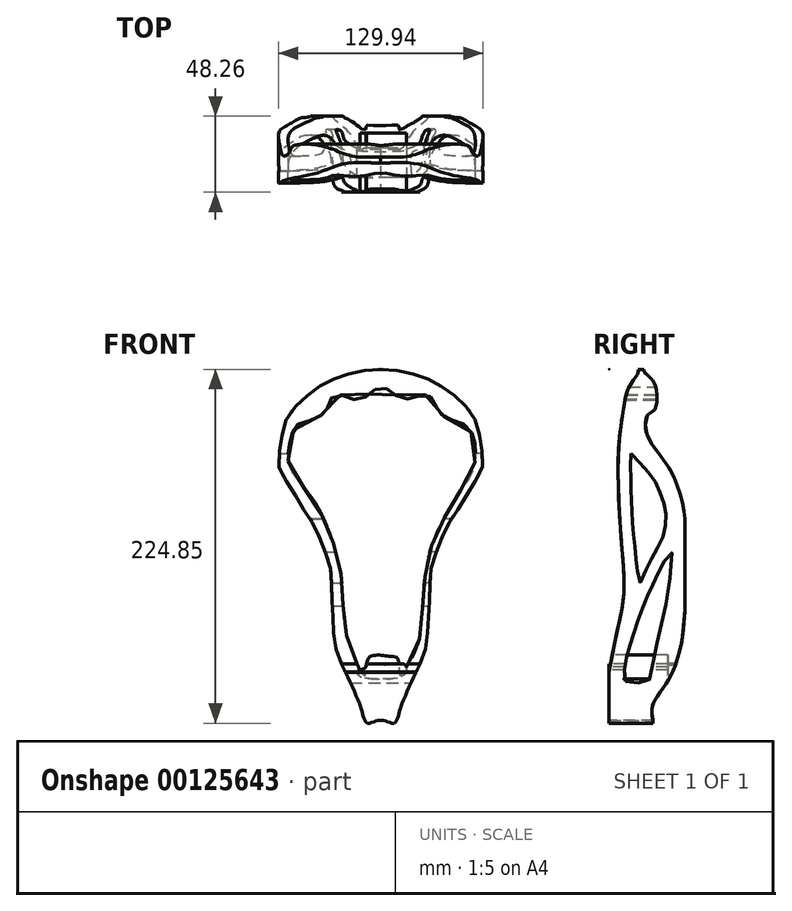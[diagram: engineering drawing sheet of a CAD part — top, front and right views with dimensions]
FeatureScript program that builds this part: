
annotation { "Feature Type Name" : "Feature", "Feature Type Description" : "" }
export const myFeature = defineFeature(function(context is Context, id is Id, definition is map)
    precondition{}
    {
        {
            var Q0;
            Q0=qCreatedBy(makeId("Front.planeOp"),FACE);
            var sketch = newSketch(context, id + "F0", { "sketchPlane" : qUnion([Q0])});
            skLineSegment(sketch, "E0", {"start": v(0, -72.83) * mm, "end": v(0, 150.24) * mm});
            skFitSpline(sketch, "E1", {"points": [v(0, 150.24) * mm, v(-1.48, 150.24) * mm, v(-4.3, 149.98) * mm, v(-9.4, 149.6) * mm, v(-12.84, 149.07) * mm, v(-16.02, 148.38) * mm, v(-20, 147.46) * mm, v(-25.8, 145.73) * mm, v(-31.7, 143.15) * mm, v(-37.82, 139.93) * mm, v(-51.56, 129.32) * mm, v(-60.43, 117.15) * mm, v(-64.43, 97.23) * mm, v(-64.26, 86.62) * mm, v(-56.78, 74.44) * mm, v(-49.65, 62.1) * mm, v(-45.82, 57.27) * mm, v(-39.73, 45.1) * mm, v(-34.34, 31.7) * mm, v(-31.9, 23.35) * mm, v(-31.04, 8.22) * mm, v(-30.34, -6.4) * mm, v(-28.43, -27.02) * mm, v(-20.77, -45.63) * mm, v(-13.64, -61.98) * mm, v(-11.9, -67.02) * mm, v(-10.34, -72.06) * mm, v(-8.43, -74.5) * mm, v(-4.95, -73.8) * mm, v(-1.64, -72.76) * mm, v(0, -72.83) * mm], "startDerivative": vector(-100.07, 3.17) * mm, "endDerivative": vector(103.4, -15.38) * mm});
            skSolve(sketch);
        }
        {
            var Q0;
            Q0=makeQuery(id+"F0.imprint","IMPRINT",FACE,{"disambiguationData":[TD([[makeQuery(id+"F0.imprint","IMPRINT",EDGE,{"derivedFrom":sQuery(id+"F0.wireOp",EDGE,"E0")}),1.0]])]});
            extrude(context, id + "F1", {"entities" : qUnion([Q0]), "oppositeDirection" : true, "depth" : 48.26 * mm});
        }
        {
            var Q0;
            Q0=makeQuery(id+"F1.opExtrude","SWEPT_BODY",BODY,{"disambiguationData":[OSD([sQuery(id+"F0.wireOp",EDGE,"E0"),sQuery(id+"F0.wireOp",EDGE,"E1")])]});
            var Q1;
            Q1=qCreatedBy(makeId("Right.planeOp"),FACE);
            mirror(context, id + "F2", {"operationType" : NewBodyOperationType.ADD, "entities" : qUnion([Q0]), "mirrorPlane" : qUnion([Q1])});
        }
        {
            var Q0;
            Q0=qCreatedBy(makeId("Right.planeOp"),FACE);
            var sketch = newSketch(context, id + "F3", { "sketchPlane" : qUnion([Q0])});
            skFitSpline(sketch, "E2", {"points": [v(0, -42.42) * mm, v(5.3, -15.25) * mm, v(8.62, 0) * mm, v(9.61, 14.25) * mm, v(7.95, 40.43) * mm, v(6.3, 64.3) * mm, v(6.05, 74.12) * mm, v(5.88, 81.69) * mm, v(5.88, 93.93) * mm, v(6.31, 104) * mm, v(8.94, 124.32) * mm, v(13.96, 141.36) * mm, v(18.55, 150.1) * mm, v(0, 150.26) * mm, v(0, -36.86) * mm, v(0, -42.42) * mm]});
            skSolve(sketch);
        }
        {
            var Q0;
            Q0=qCreatedBy(makeId("Right.planeOp"),FACE);
            var sketch = newSketch(context, id + "F4", { "sketchPlane" : qUnion([Q0])});
            skFitSpline(sketch, "E3", {"points": [v(10.32, -47.88) * mm, v(24.23, -48.44) * mm, v(25.9, -46.5) * mm, v(30.62, -23.4) * mm, v(37.02, 5.8) * mm, v(39.25, 24.16) * mm, v(39.53, 34.17) * mm, v(32.3, 22.77) * mm, v(20.8, -2.5) * mm, v(16.03, -16.67) * mm, v(13.18, -25.3) * mm, v(10.15, -38.42) * mm, v(9.43, -46.35) * mm, v(10.32, -47.88) * mm]});
            skSolve(sketch);
        }
        {
            var Q0;
            Q0 = qSketchRegion(id + "F4", true);
            extrude(context, id + "F5", {"entities" : qUnion([Q0]), "operationType" : NewBodyOperationType.REMOVE, "endBound" : BoundingType.SYMMETRIC, "oppositeDirection" : true, "depth" : 127 * mm});
        }
        {
            var Q0;
            Q0=qCreatedBy(makeId("Right.planeOp"),FACE);
            var sketch = newSketch(context, id + "F6", { "sketchPlane" : qUnion([Q0])});
            skFitSpline(sketch, "E4", {"points": [v(13.88, 96.8) * mm, v(13.72, 83.36) * mm, v(14.2, 67.88) * mm, v(15.62, 45.6) * mm, v(17.51, 27.12) * mm, v(19.25, 14.55) * mm, v(21.78, 19.3) * mm, v(28.89, 33.2) * mm, v(34.1, 43.3) * mm, v(36.16, 55) * mm, v(34.26, 67) * mm, v(27.78, 81.38) * mm, v(22.4, 87.86) * mm, v(16.09, 94.97) * mm, v(14.62, 96.3) * mm, v(13.88, 96.8) * mm]});
            skSolve(sketch);
        }
        {
            var Q0;
            Q0 = qSketchRegion(id + "F6", true);
            extrude(context, id + "F7", {"entities" : qUnion([Q0]), "operationType" : NewBodyOperationType.REMOVE, "endBound" : BoundingType.SYMMETRIC, "depth" : 152.4 * mm});
        }
        {
            var Q0;
            Q0=qCreatedBy(makeId("Right.planeOp"),FACE);
            var sketch = newSketch(context, id + "F8", { "sketchPlane" : qUnion([Q0])});
            skFitSpline(sketch, "E5", {"points": [v(48.29, 55.32) * mm, v(47.36, 62.26) * mm, v(44.82, 71.9) * mm, v(39.67, 84.9) * mm, v(28.84, 100.6) * mm, v(23.15, 112.51) * mm, v(25.05, 121.72) * mm, v(28.57, 123.88) * mm, v(30.47, 134.44) * mm, v(26.4, 144.73) * mm, v(22.34, 150.42) * mm, v(48.6, 150.15) * mm, v(48.29, 55.32) * mm]});
            skSolve(sketch);
        }
        {
            var Q0;
            Q0=makeQuery(id+"F8.imprint","IMPRINT",FACE,{"disambiguationData":[TD([[makeQuery(id+"F8.imprint","IMPRINT",EDGE,{"derivedFrom":sQuery(id+"F8.wireOp",EDGE,"E5")}),-1.0]])]});
            extrude(context, id + "F9", {"entities" : qUnion([Q0]), "operationType" : NewBodyOperationType.REMOVE, "endBound" : BoundingType.SYMMETRIC, "depth" : 152.4 * mm});
        }
        {
            var Q0;
            Q0=qCreatedBy(makeId("Front.planeOp"),FACE);
            var sketch = newSketch(context, id + "F10", { "sketchPlane" : qUnion([Q0])});
            skFitSpline(sketch, "E6", {"points": [v(12.08, -44) * mm, v(14.73, -41.19) * mm, v(19.87, -32.9) * mm, v(25.01, -18.46) * mm, v(26.18, -4.7) * mm, v(27.2, 7.62) * mm, v(27.97, 18.2) * mm, v(31.56, 35.9) * mm, v(38.5, 52.33) * mm, v(48.5, 70.03) * mm, v(57.99, 84.9) * mm, v(60.1, 96.01) * mm, v(59.08, 106.28) * mm, v(54.2, 114.49) * mm, v(44.45, 118.34) * mm, v(39.32, 120.64) * mm, v(36.5, 124.24) * mm, v(31.37, 132.96) * mm, v(28.55, 134.24) * mm, v(21.88, 132.7) * mm, v(14.44, 131.42) * mm, v(7.77, 135.27) * mm, v(0, 138.86) * mm, v(-8.4, 133.73) * mm, v(-15.84, 130.9) * mm, v(-23.54, 133.22) * mm, v(-28.4, 133.99) * mm, v(-31.49, 131.93) * mm, v(-32.77, 127.83) * mm, v(-36.36, 122.44) * mm, v(-43.03, 118.34) * mm, v(-50.22, 116.54) * mm, v(-55.6, 111.4) * mm, v(-58.17, 101.66) * mm, v(-58.17, 89.6) * mm, v(-47.14, 72.92) * mm, v(-38.67, 60.35) * mm, v(-30.46, 40.6) * mm, v(-24.82, 15.97) * mm, v(-22.77, -13.54) * mm, v(-16.6, -32.78) * mm, v(-11.99, -42.79) * mm, v(-9.94, -44.07) * mm, v(-8.91, -36.89) * mm, v(-5.58, -36.89) * mm, v(-2.24, -37.14) * mm, v(5.97, -37.14) * mm, v(10.84, -36.63) * mm, v(12.08, -44) * mm]});
            skSolve(sketch);
        }
        {
            var Q0;
            Q0=makeQuery(id+"F10.imprint","IMPRINT",FACE,{"disambiguationData":[TD([[makeQuery(id+"F10.imprint","IMPRINT",EDGE,{"derivedFrom":sQuery(id+"F10.wireOp",EDGE,"E6")}),1.0]])]});
            extrude(context, id + "F11", {"entities" : qUnion([Q0]), "operationType" : NewBodyOperationType.REMOVE, "endBound" : BoundingType.SYMMETRIC, "depth" : 228.6 * mm});
        }
        {
            var Q0;
            Q0=qCreatedBy(makeId("Right.planeOp"),FACE);
            var sketch = newSketch(context, id + "F12", { "sketchPlane" : qUnion([Q0])});
            skFitSpline(sketch, "E7", {"points": [v(48.25, -0.25) * mm, v(48.37, -74.61) * mm, v(28, -74.61) * mm, v(28.06, -73.94) * mm, v(27.6, -70.58) * mm, v(27.19, -66.2) * mm, v(27.8, -62.78) * mm, v(31.96, -55.58) * mm, v(36.87, -48.65) * mm, v(40.5, -41.86) * mm, v(42.46, -37.02) * mm, v(45.28, -26.91) * mm, v(46.7, -19.31) * mm, v(47.97, -6.06) * mm, v(48.24, -2.3) * mm, v(48.25, -0.25) * mm]});
            skSolve(sketch);
        }
        {
            var Q0;
            Q0 = qSketchRegion(id + "F12", true);
            extrude(context, id + "F13", {"entities" : qUnion([Q0]), "operationType" : NewBodyOperationType.REMOVE, "endBound" : BoundingType.SYMMETRIC, "depth" : 228.6 * mm});
        }
        {
            var Q0;
            Q0=qCreatedBy(makeId("Front.planeOp"),FACE);
            var sketch = newSketch(context, id + "F14", { "sketchPlane" : qUnion([Q0])});
            skFitSpline(sketch, "E8", {"points": [v(-10.04, -39.49) * mm, v(-7.93, -33.4) * mm, v(0, -31.3) * mm, v(6.09, -32.08) * mm, v(10.32, -32.88) * mm, v(11.9, -36.31) * mm, v(15.34, -37.37) * mm, v(15.08, -43.45) * mm, v(-4.76, -46.36) * mm, v(-13.48, -44.51) * mm, v(-15.33, -41.34) * mm, v(-10.04, -39.49) * mm]});
            skSolve(sketch);
        }
        {
            var Q0;
            Q0=makeQuery(id+"F14.imprint","IMPRINT",FACE,{"disambiguationData":[TD([[makeQuery(id+"F14.imprint","IMPRINT",EDGE,{"derivedFrom":sQuery(id+"F14.wireOp",EDGE,"E8")}),-1.0]])]});
            extrude(context, id + "F15", {"entities" : qUnion([Q0]), "operationType" : NewBodyOperationType.ADD, "oppositeDirection" : true, "depth" : 37.46 * mm});
        }
        {
            var Q0;
            Q0=makeQuery(id+"F3.imprint","IMPRINT",FACE,{"disambiguationData":[TD([[makeQuery(id+"F3.imprint","IMPRINT",EDGE,{"derivedFrom":sQuery(id+"F3.wireOp",EDGE,"E2")}),1.0]])]});
            extrude(context, id + "F16", {"entities" : qUnion([Q0]), "operationType" : NewBodyOperationType.REMOVE, "endBound" : BoundingType.SYMMETRIC, "depth" : 228.6 * mm});
        }
    });
